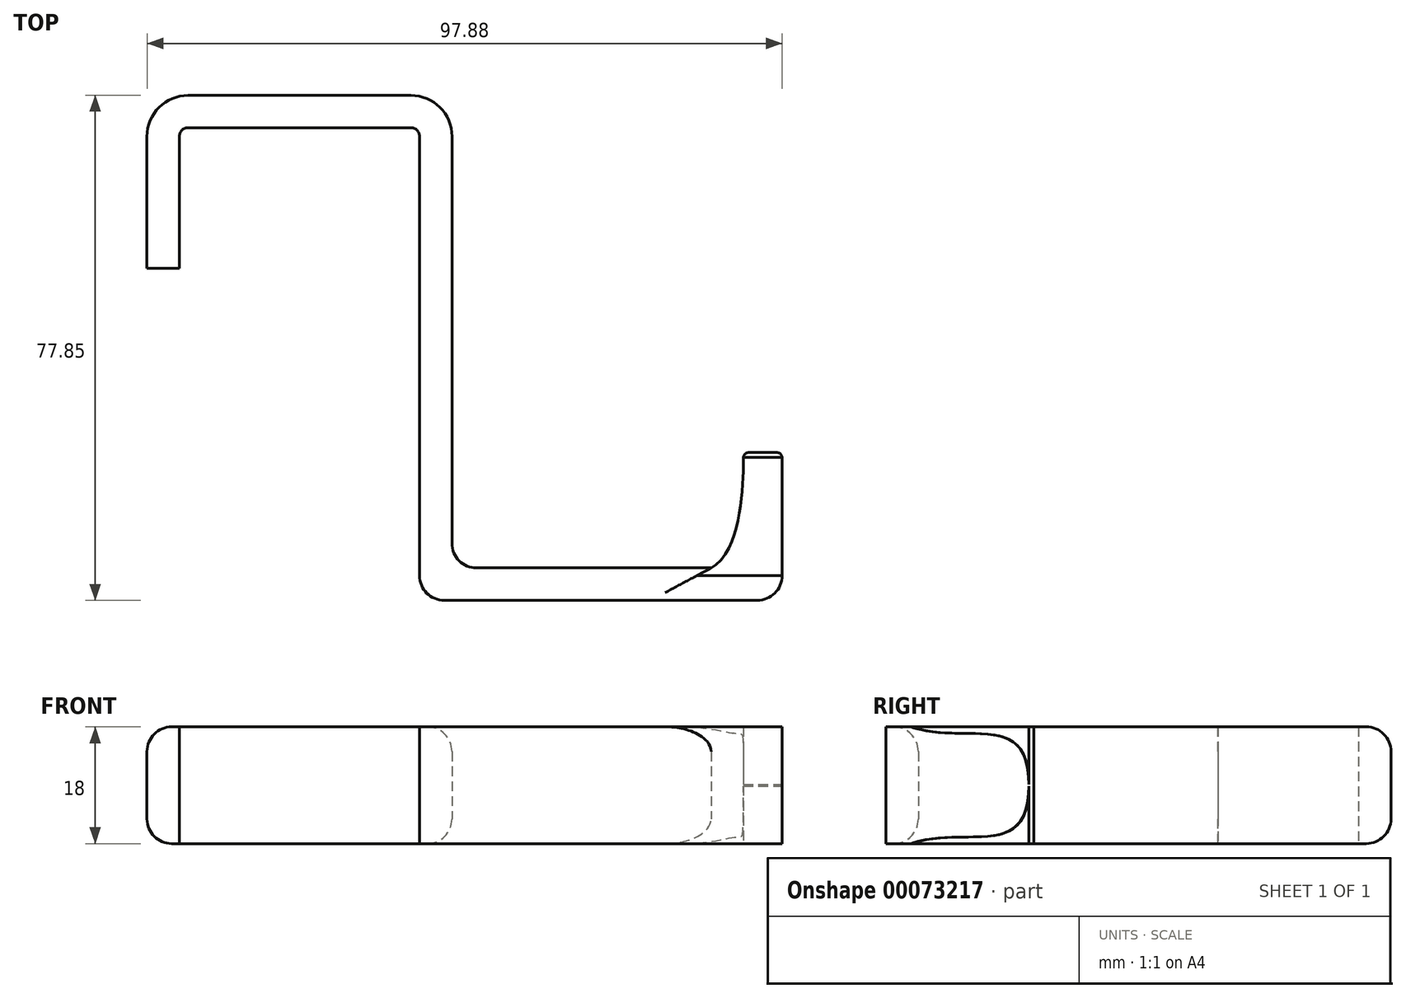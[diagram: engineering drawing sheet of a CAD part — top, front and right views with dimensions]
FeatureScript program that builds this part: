
annotation { "Feature Type Name" : "Feature", "Feature Type Description" : "" }
export const myFeature = defineFeature(function(context is Context, id is Id, definition is map)
    precondition{}
    {
        {
            var Q0;
            Q0=qCreatedBy(makeId("Top.planeOp"),FACE);
            var sketch = newSketch(context, id + "F0", { "sketchPlane" : qUnion([Q0])});
            skPoint(sketch, "E0.rect.middle", {"position": v(0, 0) * mm});
            skLineSegment(sketch, "E1.top", {"start": v(3.17, 26.67) * mm, "end": v(37.47, 26.67) * mm});
            skLineSegment(sketch, "E1.left", {"start": v(-3.17, 17.78) * mm, "end": v(-3.17, 20.32) * mm});
            skLineSegment(sketch, "E1.right", {"start": v(43.82, 20.32) * mm, "end": v(43.82, 21.67) * mm});
            skLineSegment(sketch, "E2.left", {"start": v(43.82, 21.67) * mm, "end": v(43.83, -42.37) * mm});
            skPoint(sketch, "E3.visualSharp", {"position": v(-3.18, 26.67) * mm});
            skArc(sketch, "E3.filletArc", {"start": v(3.17, 26.67) * mm, "mid": v(-1.32, 24.81) * mm, "end": v(-3.18, 20.32) * mm});
            skPoint(sketch, "E4.visualSharp", {"position": v(43.82, 26.67) * mm});
            skArc(sketch, "E4.filletArc", {"start": v(43.83, 20.32) * mm, "mid": v(41.97, 24.81) * mm, "end": v(37.47, 26.67) * mm});
            skLineSegment(sketch, "E5", {"start": v(38.83, -42.3) * mm, "end": v(38.83, -47.37) * mm});
            skLineSegment(sketch, "E6", {"start": v(42.64, -51.18) * mm, "end": v(90.9, -51.18) * mm});
            skLineSegment(sketch, "E7", {"start": v(94.7, -47.37) * mm, "end": v(94.7, -46.18) * mm});
            skLineSegment(sketch, "E8", {"start": v(94.7, -46.18) * mm, "end": v(47.64, -46.18) * mm});
            skLineSegment(sketch, "E9", {"start": v(94.7, -46.18) * mm, "end": v(94.7, -28.4) * mm});
            skLineSegment(sketch, "E10", {"start": v(94.7, -28.4) * mm, "end": v(88.76, -28.4) * mm});
            skFitSpline(sketch, "E11", {"points": [v(88.76, -28.4) * mm, v(83.77, -46.18) * mm], "startDerivative": vector(-0.08, -13.6) * mm, "endDerivative": vector(-14.55, -7.82) * mm});
            skPoint(sketch, "E12.visualSharp", {"position": v(38.83, -51.18) * mm});
            skArc(sketch, "E12.filletArc", {"start": v(38.83, -47.37) * mm, "mid": v(39.94, -50.07) * mm, "end": v(42.64, -51.18) * mm});
            skPoint(sketch, "E13.visualSharp", {"position": v(94.7, -51.18) * mm});
            skArc(sketch, "E13.filletArc", {"start": v(90.9, -51.18) * mm, "mid": v(93.59, -50.07) * mm, "end": v(94.7, -47.37) * mm});
            skPoint(sketch, "E14.visualSharp", {"position": v(43.83, -46.18) * mm});
            skArc(sketch, "E14.filletArc", {"start": v(43.83, -42.37) * mm, "mid": v(44.94, -45.07) * mm, "end": v(47.64, -46.18) * mm});
            skLineSegment(sketch, "E15", {"start": v(-3.17, 17.78) * mm, "end": v(-3.17, 0) * mm});
            skLineSegment(sketch, "E16", {"start": v(-3.17, 0) * mm, "end": v(1.83, 0) * mm});
            skLineSegment(sketch, "E17", {"start": v(1.83, 20.4) * mm, "end": v(1.83, 0) * mm});
            skLineSegment(sketch, "E18", {"start": v(38.82, -42.3) * mm, "end": v(38.82, 20.4) * mm});
            skLineSegment(sketch, "E19", {"start": v(37.55, 21.67) * mm, "end": v(3.1, 21.67) * mm});
            skLineSegment(sketch, "E20", {"start": v(43.82, 21.67) * mm, "end": v(38.82, 21.67) * mm});
            skPoint(sketch, "E21.visualSharp", {"position": v(1.83, 21.67) * mm});
            skArc(sketch, "E21.filletArc", {"start": v(3.1, 21.67) * mm, "mid": v(2.2, 21.3) * mm, "end": v(1.83, 20.4) * mm});
            skPoint(sketch, "E22.visualSharp", {"position": v(38.82, 21.67) * mm});
            skArc(sketch, "E22.filletArc", {"start": v(38.82, 20.4) * mm, "mid": v(38.45, 21.3) * mm, "end": v(37.55, 21.67) * mm});
            skSolve(sketch);
        }
        {
            var Q0;
            Q0=makeQuery(id+"F0.imprint","IMPRINT",FACE,{"disambiguationData":[TD([[makeQuery(id+"F0.imprint","IMPRINT",EDGE,{"derivedFrom":sQuery(id+"F0.wireOp",EDGE,"E1.top")}),-1.0]])]});
            var Q1;
            {var subQ0=sQuery(id+"F0.wireOp",EDGE,"E9");Q1=makeQuery(id+"F0.imprint","IMPRINT",FACE,{"disambiguationData":[TD([[makeQuery(id+"F0.imprint","IMPRINT",EDGE,{"derivedFrom":subQ0}),1.0]])]});}
            extrude(context, id + "F1", {"entities" : qUnion([Q0, Q1]), "depth" : 18 * mm});
        }
        {
            var Q0;
            Q0=makeQuery(id+"F1.opExtrude","CAP_EDGE",EDGE,{"disambiguationData":[OSD([sQuery(id+"F0.wireOp",EDGE,"E1.right"),sQuery(id+"F0.wireOp",EDGE,"E2.left")])],"isStart":false});
            var Q1;
            Q1=makeQuery(id+"F1.opExtrude","CAP_EDGE",EDGE,{"disambiguationData":[OSD([sQuery(id+"F0.wireOp",EDGE,"E1.right"),sQuery(id+"F0.wireOp",EDGE,"E2.left")])],"isStart":true});
            fillet(context, id + "F2", {"entities" : qUnion([Q0, Q1]), "radius" : 3.8 * mm, "tangentPropagation" : true, "allowEdgeOverflow" : false});
        }
        {
            var Q0;
            Q0=makeQuery(id+"FA34ARAimiPUhsl_1.boolean.opBoolean","INTERSECT",EDGE,{"derivedFrom":[makeQuery(id+"F1.opExtrude","SWEPT_FACE",FACE,{"disambiguationData":[OSD([sQuery(id+"F0.wireOp",EDGE,"E11")])]}),makeQuery(id+"FA34ARAimiPUhsl_1.opExtrude","SWEPT_FACE",FACE,{"disambiguationData":[OSD([sQuery(id+"FN3c6OtnZbbg9VR_1.wireOp",EDGE,"6ef33ffa-1e93-43d1-8b5c-53580aea4be20.MirrorCS")])]})]});
            var Q1;
            Q1=makeQuery(id+"F1.opExtrude","SWEPT_EDGE",EDGE,{"disambiguationData":[OSD([sQuery(id+"F0.wireOp",EDGE,"E10"),sQuery(id+"F0.wireOp",EDGE,"E11")])]});
            var Q2;
            Q2=makeQuery(id+"FA34ARAimiPUhsl_1.boolean.opBoolean","INTERSECT",EDGE,{"derivedFrom":[makeQuery(id+"F1.opExtrude","SWEPT_FACE",FACE,{"disambiguationData":[OSD([sQuery(id+"F0.wireOp",EDGE,"E11")])]}),makeQuery(id+"FA34ARAimiPUhsl_1.opExtrude","SWEPT_FACE",FACE,{"disambiguationData":[OSD([sQuery(id+"FN3c6OtnZbbg9VR_1.wireOp",EDGE,"0fe96e33-9b14-41ff-846c-9319032674f4")])]})]});
            var Q3;
            Q3=makeQuery(id+"FA34ARAimiPUhsl_1.boolean.opBoolean","COPY",EDGE,{"derivedFrom":makeQuery(id+"FA34ARAimiPUhsl_1.opExtrude","CAP_EDGE",EDGE,{"disambiguationData":[OSD([sQuery(id+"FN3c6OtnZbbg9VR_1.wireOp",EDGE,"6ef33ffa-1e93-43d1-8b5c-53580aea4be20.MirrorCS")])],"isStart":true})});
            var Q4;
            Q4=makeQuery(id+"F1.opExtrude","SWEPT_EDGE",EDGE,{"disambiguationData":[OSD([sQuery(id+"F0.wireOp",EDGE,"E9"),sQuery(id+"F0.wireOp",EDGE,"E10")])]});
            var Q5;
            Q5=makeQuery(id+"FA34ARAimiPUhsl_1.boolean.opBoolean","COPY",EDGE,{"derivedFrom":makeQuery(id+"FA34ARAimiPUhsl_1.opExtrude","CAP_EDGE",EDGE,{"disambiguationData":[OSD([sQuery(id+"FN3c6OtnZbbg9VR_1.wireOp",EDGE,"0fe96e33-9b14-41ff-846c-9319032674f4")])],"isStart":true})});
            fillet(context, id + "F3", {"entities" : qUnion([Q0, Q1, Q2, Q3, Q4, Q5]), "radius" : 0.76 * mm, "tangentPropagation" : true, "allowEdgeOverflow" : false});
        }
        {
            var Q0;
            Q0=makeQuery(id+"F1.opExtrude","SWEPT_FACE",FACE,{"disambiguationData":[OSD([sQuery(id+"F0.wireOp",EDGE,"E7"),sQuery(id+"F0.wireOp",EDGE,"E9")])]});
            var sketch = newSketch(context, id + "F4", { "sketchPlane" : qUnion([Q0])});
            skLineSegment(sketch, "E23", {"start": v(-29.17, 18) * mm, "end": v(-47.37, 18) * mm});
            skLineSegment(sketch, "E24", {"start": v(-47.37, 18) * mm, "end": v(-47.37, 0) * mm});
            skLineSegment(sketch, "E25", {"start": v(-47.37, 0) * mm, "end": v(-29.17, 0) * mm});
            skLineSegment(sketch, "E26", {"start": v(-29.17, 0) * mm, "end": v(-29.17, 18) * mm});
            skLineSegment(sketch, "E27", {"start": v(-29.17, 9) * mm, "end": v(-47.37, 9) * mm});
            skFitSpline(sketch, "E28", {"points": [v(-47.37, 18) * mm, v(-29.17, 9) * mm], "startDerivative": vector(26.2, -8.72) * mm, "endDerivative": vector(-0.1, -35.25) * mm});
            skFitSpline(sketch, "E29.MirrorCS", {"points": [v(-47.37, 0) * mm, v(-29.17, 9) * mm], "startDerivative": vector(26.2, 8.72) * mm, "endDerivative": vector(-0.1, 35.25) * mm});
            skSolve(sketch);
        }
        {
            var Q0;
            {var subQ0=sQuery(id+"F4.wireOp",EDGE,"E23");Q0=makeQuery(id+"F4.imprint","IMPRINT",FACE,{"disambiguationData":[TD([[makeQuery(id+"F4.imprint","IMPRINT",EDGE,{"derivedFrom":subQ0}),-1.0]])]});}
            var Q1;
            {var subQ0=sQuery(id+"F4.wireOp",EDGE,"E25");Q1=makeQuery(id+"F4.imprint","IMPRINT",FACE,{"disambiguationData":[TD([[makeQuery(id+"F4.imprint","IMPRINT",EDGE,{"derivedFrom":subQ0}),1.0]])]});}
            extrude(context, id + "F5", {"entities" : qUnion([Q0, Q1]), "operationType" : NewBodyOperationType.REMOVE, "oppositeDirection" : true, "depth" : 15 * mm});
        }
    });
